# Revit family: HEM
name_source: partatom
category: Lighting Fixtures
revit_build: Autodesk Revit Architecture 2012 (Build: 20110309_2315(x64)
units: mm (PartAtom-declared; Revit-internal decimal feet)

## types (6) — shared parameters
Backbox = Plastic - Hubbell - White
Color Filter = 16777215
Connector Description = Lighting
Default Elevation = 48 "
Description = HEM is an enclosed and gasketed hazardous location LED product.
Dimming Lamp Color Temperature Shift = <None>
Emit Shape Visible in Rendering = Yes
Emit from Rectangle Length = 48 "
Emit from Rectangle Width = 5.78 "
Glass = Glass - Hubbell - Frosted Lens
Lamp = LED Hazardous Location Enclosed and Gasketed
Manufacturer = Columbia Lighting
Manufacturer Fax = (866)-898-1065
Model = HEM
Product Documentation Link = http://cdn.columbialighting.com
Product Page URL = http://www.columbialighting.com
Row Length = 48 "
Tilt Angle = -90.00°
URL = http://www.columbialighting.com
Voltage = 120 V

## per-type parameters (varying)
| type | Apparent Load | Lens | Lumen Output | Photometric Web File | Shielding | Wattage Comments |
| HEM4-40HL-DFA-EU | 54 VA | Lens : DFA Lens | High Lumen | HEM4-40HL-DFA-EU.IES | Deep Frosted Acrylic | 54W |
| HEM4-40HL-RFA-EU | 54 VA | Lens : RFA Lens | High Lumen | HEM4-40HL-RFA-EU.IES | Ribbed Frosted Acrylic | 54W |
| HEM4-40ML-DFA-EU | 54 VA | Lens : DFA Lens | Medium Lumen | HEM4-40HL-RFA-EU.IES | Deep Frosted Acrylic | 46W |
| HEM4-40ML-RFA-EU | 54 VA | Lens : RFA Lens | Medium Lumen | HEM4-40ML-RFA-EU.IES | Ribbed Frosted Acrylic | 46W |
| HEM4-40VL-DFA-EU | 68 VA | Lens : DFA Lens | Very High Lumen | HEM4-40VL-DFA-EU.IES | Deep Frosted Acrylic | 68W |
| HEM4-40VL-RFA-EU | 68 VA | Lens : RFA Lens | Very High Lumen | HEM4-40VL-RFA-EU.IES | Ribbed Frosted Acrylic | 68W |

## geometry (parser evidence)
native form markers: Blend x4, Sweep x4
no freeform markers — native parametric forms only
